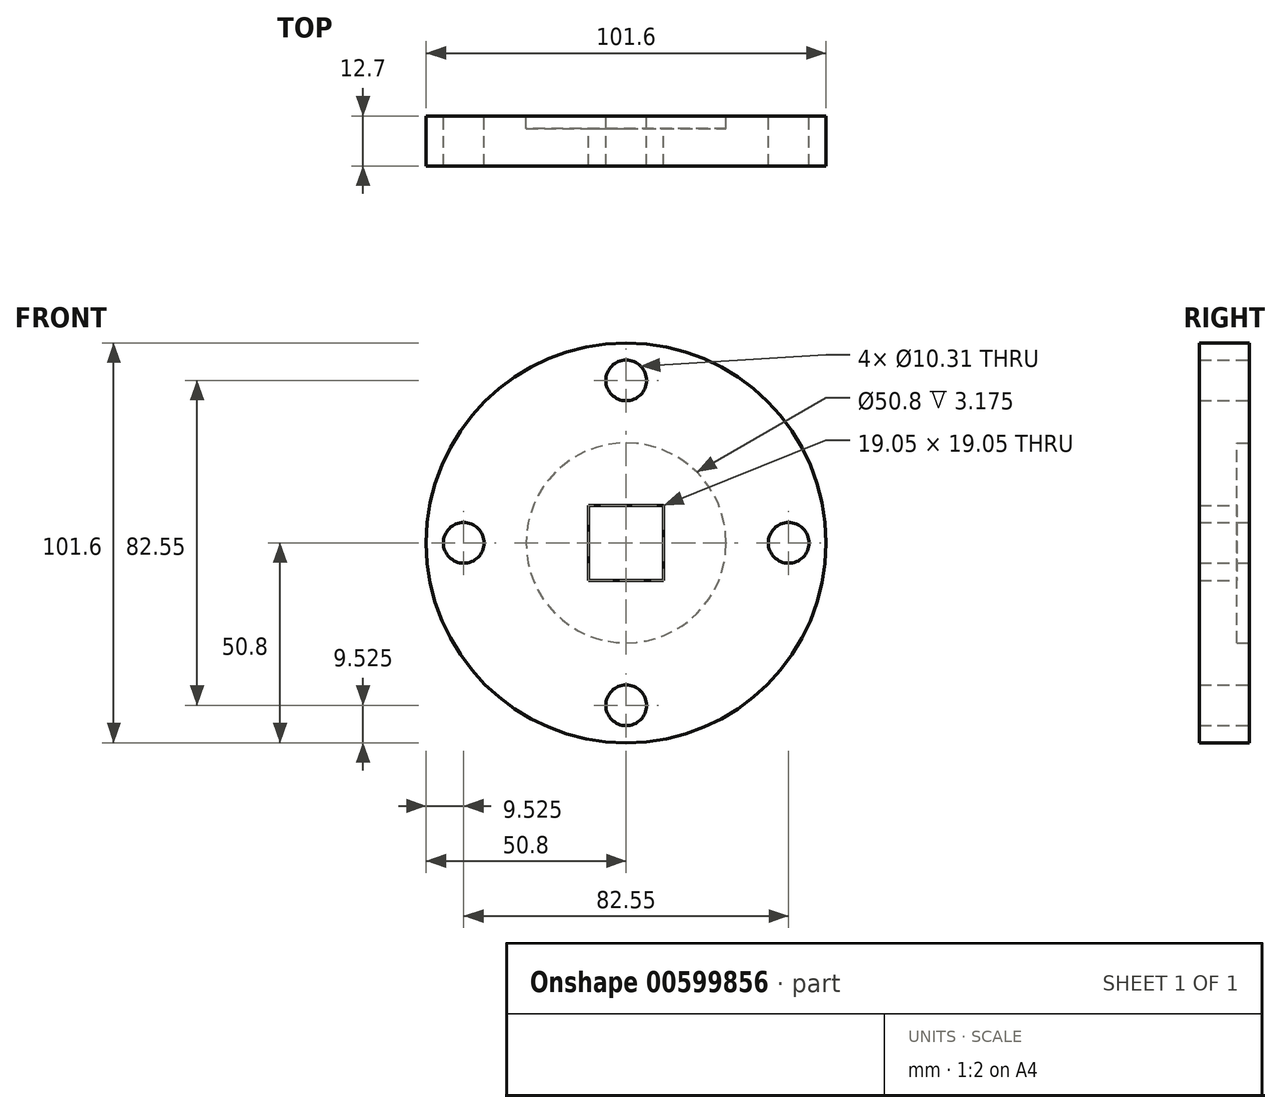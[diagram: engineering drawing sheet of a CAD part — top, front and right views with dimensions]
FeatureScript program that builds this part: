
annotation { "Feature Type Name" : "Feature", "Feature Type Description" : "" }
export const myFeature = defineFeature(function(context is Context, id is Id, definition is map)
    precondition{}
    {
        {
            var Q0;
            Q0=qCreatedBy(makeId("Front.planeOp"),FACE);
            var sketch = newSketch(context, id + "F0", { "sketchPlane" : qUnion([Q0])});
            skCircle(sketch, "E0", {"center": v(0, 0) * mm, "radius": 50.8 * mm});
            skCircle(sketch, "E1", {"center": v(0, 41.28) * mm, "radius": 5.16 * mm});
            skCircle(sketch, "E2", {"center": v(-41.28, 0) * mm, "radius": 5.16 * mm});
            skCircle(sketch, "E3", {"center": v(41.28, 0) * mm, "radius": 5.16 * mm});
            skCircle(sketch, "E4", {"center": v(0, -41.28) * mm, "radius": 5.16 * mm});
            skLineSegment(sketch, "E5.bottom", {"start": v(-9.52, 9.52) * mm, "end": v(9.53, 9.52) * mm});
            skLineSegment(sketch, "E5.top", {"start": v(-9.53, -9.53) * mm, "end": v(9.53, -9.53) * mm});
            skLineSegment(sketch, "E5.left", {"start": v(-9.52, 9.52) * mm, "end": v(-9.53, -9.53) * mm});
            skLineSegment(sketch, "E5.right", {"start": v(9.53, 9.52) * mm, "end": v(9.53, -9.53) * mm});
            skSolve(sketch);
        }
        {
            var Q0;
            Q0 = qSketchRegion(id + "F0", true);
            extrude(context, id + "F1", {"entities" : qUnion([Q0]), "depth" : 12.7 * mm, "offsetDistance" : 25.4 * mm});
        }
        {
            var Q0;
            Q0=qCreatedBy(makeId("Front.planeOp"),FACE);
            var sketch = newSketch(context, id + "F2", { "sketchPlane" : qUnion([Q0])});
            skCircle(sketch, "E6", {"center": v(0, 0) * mm, "radius": 25.4 * mm});
            skSolve(sketch);
        }
        {
            var Q0;
            Q0 = qSketchRegion(id + "F2", true);
            extrude(context, id + "F3", {"entities" : qUnion([Q0]), "operationType" : NewBodyOperationType.REMOVE, "depth" : 3.17 * mm, "offsetDistance" : 25.4 * mm});
        }
    });
